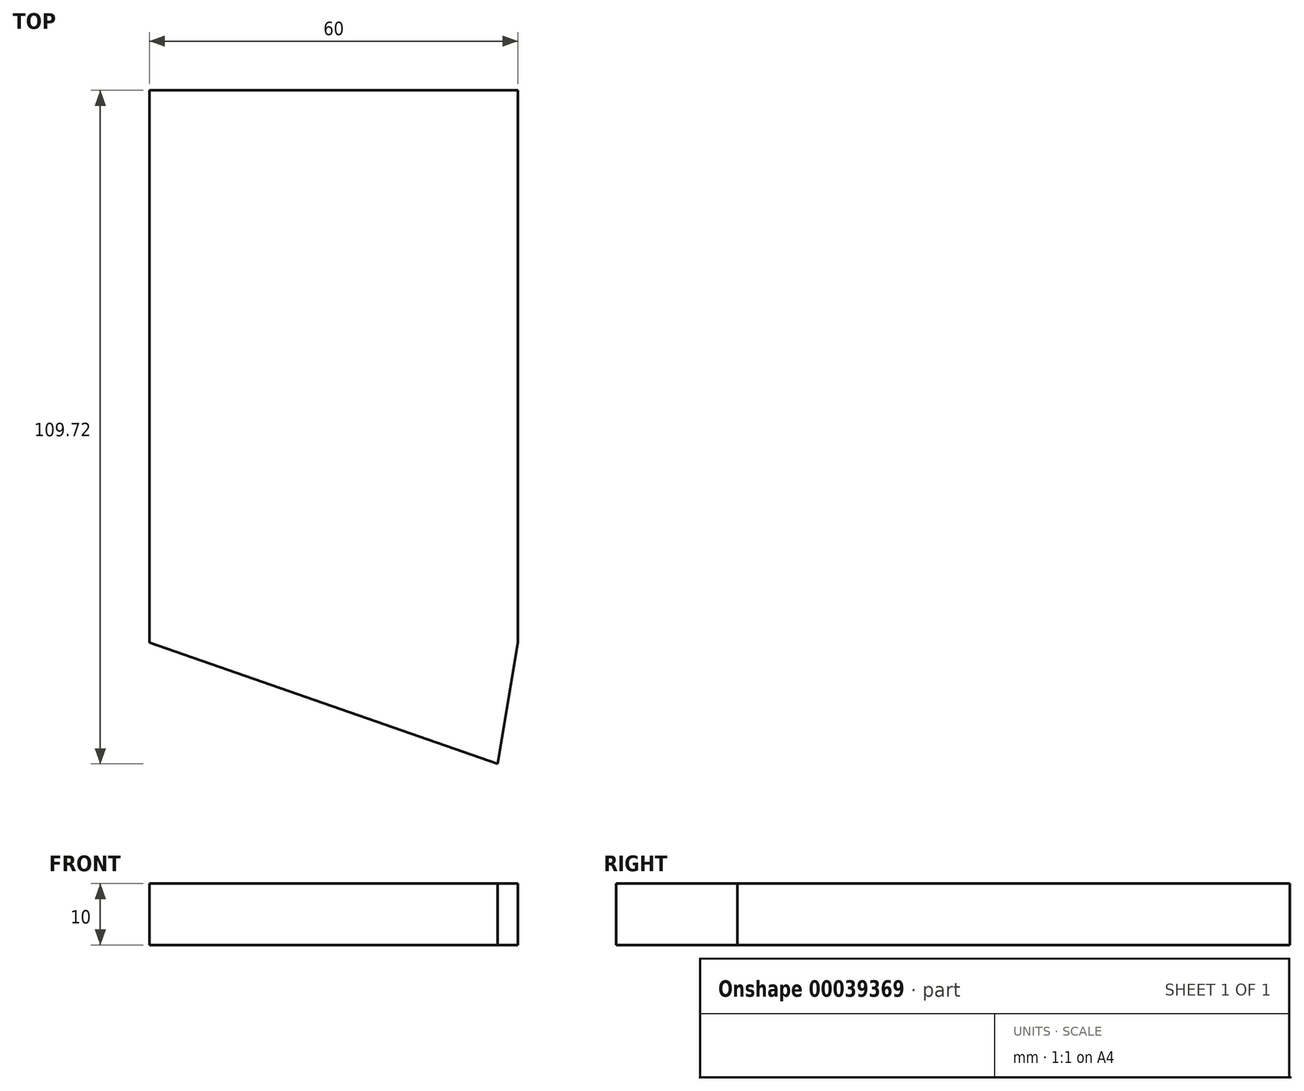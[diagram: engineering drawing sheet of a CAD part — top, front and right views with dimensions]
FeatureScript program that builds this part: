
annotation { "Feature Type Name" : "Feature", "Feature Type Description" : "" }
export const myFeature = defineFeature(function(context is Context, id is Id, definition is map)
    precondition{}
    {
        {
            var Q0;
            Q0=qCreatedBy(makeId("Top.planeOp"),FACE);
            var sketch = newSketch(context, id + "F0", { "sketchPlane" : qUnion([Q0])});
            skLineSegment(sketch, "E0.bottom", {"start": v(-46.92, 37.61) * mm, "end": v(13.08, 37.61) * mm});
            skLineSegment(sketch, "E0.top", {"start": v(-46.92, -7.39) * mm, "end": v(13.08, -7.39) * mm});
            skLineSegment(sketch, "E0.left", {"start": v(-46.92, 37.61) * mm, "end": v(-46.92, -7.39) * mm});
            skLineSegment(sketch, "E0.right", {"start": v(13.08, 37.61) * mm, "end": v(13.08, -7.39) * mm});
            skLineSegment(sketch, "E1.top", {"start": v(-46.92, -52.39) * mm, "end": v(13.08, -52.39) * mm});
            skLineSegment(sketch, "E1.left", {"start": v(-46.92, -7.39) * mm, "end": v(-46.92, -52.39) * mm});
            skLineSegment(sketch, "E1.right", {"start": v(13.08, -7.39) * mm, "end": v(13.08, -52.39) * mm});
            skLineSegment(sketch, "E2.top", {"start": v(-41.92, 67.61) * mm, "end": v(8.08, 67.61) * mm});
            skLineSegment(sketch, "E3", {"start": v(-46.92, -52.39) * mm, "end": v(9.75, -72.1) * mm});
            skLineSegment(sketch, "E4", {"start": v(9.75, -72.1) * mm, "end": v(13.08, -52.39) * mm});
            skLineSegment(sketch, "E5", {"start": v(-46.92, 37.61) * mm, "end": v(-41.92, 67.61) * mm});
            skLineSegment(sketch, "E6", {"start": v(13.08, 37.61) * mm, "end": v(8.08, 67.61) * mm});
            skLineSegment(sketch, "E7", {"start": v(-46.92, -52.39) * mm, "end": v(11.42, -62.25) * mm, "construction": true});
            skLineSegment(sketch, "E8", {"start": v(-13.33, 37.61) * mm, "end": v(-13.33, 67.61) * mm, "construction": true});
            skSolve(sketch);
        }
        {
            var Q0;
            Q0=makeQuery(id+"F0.imprint","IMPRINT",FACE,{"disambiguationData":[TD([[makeQuery(id+"F0.imprint","IMPRINT",EDGE,{"derivedFrom":sQuery(id+"F0.wireOp",EDGE,"E0.bottom")}),1.0]])]});
            var Q1;
            Q1=makeQuery(id+"F0.imprint","IMPRINT",FACE,{"disambiguationData":[TD([[makeQuery(id+"F0.imprint","IMPRINT",EDGE,{"derivedFrom":sQuery(id+"F0.wireOp",EDGE,"E0.left")}),1.0]])]});
            var Q2;
            Q2=makeQuery(id+"F0.imprint","IMPRINT",FACE,{"disambiguationData":[TD([[makeQuery(id+"F0.imprint","IMPRINT",EDGE,{"derivedFrom":sQuery(id+"F0.wireOp",EDGE,"E0.top")}),-1.0]])]});
            var Q3;
            Q3=makeQuery(id+"F0.imprint","IMPRINT",FACE,{"disambiguationData":[TD([[makeQuery(id+"F0.imprint","IMPRINT",EDGE,{"derivedFrom":sQuery(id+"F0.wireOp",EDGE,"E1.top")}),-1.0]])]});
            extrude(context, id + "F1", {"entities" : qUnion([Q0, Q1, Q2, Q3]), "depth" : 10 * mm});
        }
    });
